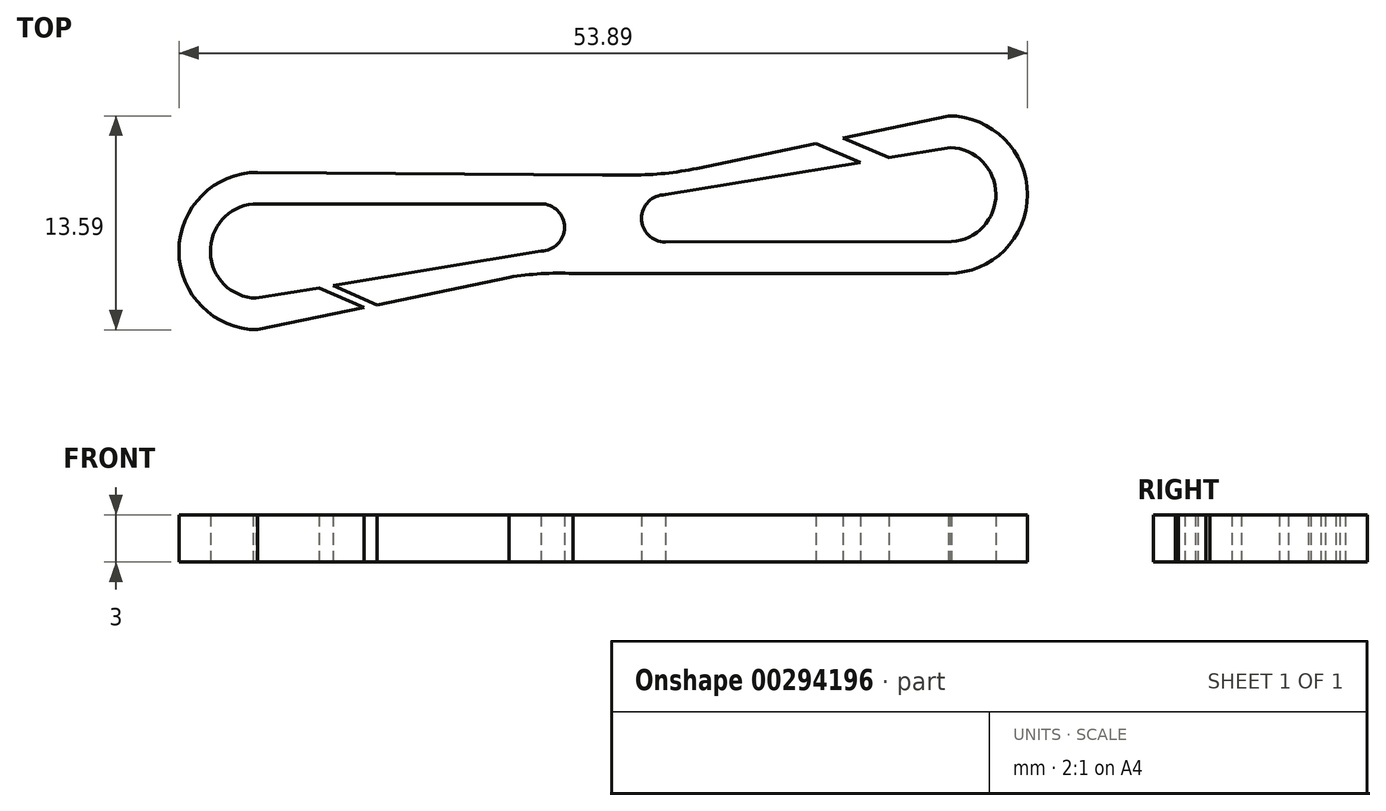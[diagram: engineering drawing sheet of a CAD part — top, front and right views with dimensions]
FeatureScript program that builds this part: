
annotation { "Feature Type Name" : "Feature", "Feature Type Description" : "" }
export const myFeature = defineFeature(function(context is Context, id is Id, definition is map)
    precondition{}
    {
        {
            var Q0;
            Q0=qCreatedBy(makeId("Top.planeOp"),FACE);
            var sketch = newSketch(context, id + "F0", { "sketchPlane" : qUnion([Q0])});
            skLineSegment(sketch, "E0.bottom", {"start": v(0, 0) * mm, "end": v(22, 0) * mm});
            skArc(sketch, "E1", {"start": v(22, 0) * mm, "mid": v(27, 5) * mm, "end": v(22, 10) * mm});
            skLineSegment(sketch, "E2.0", {"start": v(4, 0.17) * mm, "end": v(4, 6.83) * mm, "construction": true});
            skArc(sketch, "E3", {"start": v(4, 5) * mm, "mid": v(2.5, 3.5) * mm, "end": v(4, 2) * mm});
            skLineSegment(sketch, "E4", {"start": v(22, 10) * mm, "end": v(15.3, 8.61) * mm});
            skLineSegment(sketch, "E5", {"start": v(1.94, 6.26) * mm, "end": v(0, 6.26) * mm});
            skArc(sketch, "E6.0", {"start": v(22.2, 2.01) * mm, "mid": v(25, 5.05) * mm, "end": v(22.11, 8) * mm});
            skLineSegment(sketch, "E7", {"start": v(22.11, 8) * mm, "end": v(18.21, 7.36) * mm});
            skLineSegment(sketch, "E8", {"start": v(22.2, 2.01) * mm, "end": v(4, 2) * mm});
            skLineSegment(sketch, "E9", {"start": v(15.3, 8.61) * mm, "end": v(18.21, 7.36) * mm});
            skLineSegment(sketch, "E10.0", {"start": v(13.59, 8.25) * mm, "end": v(16.39, 7.05) * mm});
            skLineSegment(sketch, "E11.trimOffspring", {"start": v(13.59, 8.25) * mm, "end": v(6.02, 6.68) * mm});
            skLineSegment(sketch, "E12.trimOffspring", {"start": v(16.39, 7.05) * mm, "end": v(4, 5) * mm});
            skPoint(sketch, "E13.visualSharp", {"position": v(4, 6.26) * mm});
            skArc(sketch, "E13.filletArc", {"start": v(1.94, 6.26) * mm, "mid": v(3.99, 6.36) * mm, "end": v(6.02, 6.68) * mm});
            skArc(sketch, "E14.1.0", {"start": v(-1.84, 0) * mm, "mid": v(-3.88, -0.02) * mm, "end": v(-5.9, -0.25) * mm});
            skArc(sketch, "E14.1.1", {"start": v(-21.9, 6.42) * mm, "mid": v(-26.9, 1.42) * mm, "end": v(-21.9, -3.58) * mm});
            skArc(sketch, "E14.1.2", {"start": v(-3.9, 1.42) * mm, "mid": v(-2.4, 2.92) * mm, "end": v(-3.9, 4.42) * mm});
            skLineSegment(sketch, "E14.1.3", {"start": v(-3.9, 6.26) * mm, "end": v(-3.9, -0.4) * mm, "construction": true});
            skLineSegment(sketch, "E14.1.5", {"start": v(0, 6.26) * mm, "end": v(-21.9, 6.42) * mm});
            skLineSegment(sketch, "E14.1.6", {"start": v(-17.1, -0.76) * mm, "end": v(-3.9, 1.42) * mm});
            skPoint(sketch, "E14.1.7", {"position": v(-3.9, 0.18) * mm});
            skLineSegment(sketch, "E14.1.8", {"start": v(-21.9, -3.58) * mm, "end": v(-15.14, -2.17) * mm});
            skLineSegment(sketch, "E14.1.9", {"start": v(-1.84, 0) * mm, "end": v(0, 0) * mm});
            skArc(sketch, "E14.1.10", {"start": v(-22.17, 4.41) * mm, "mid": v(-24.89, 1.34) * mm, "end": v(-22, -1.57) * mm});
            skLineSegment(sketch, "E14.1.11", {"start": v(-22, -1.57) * mm, "end": v(-18, -0.91) * mm});
            skLineSegment(sketch, "E14.1.12", {"start": v(-22.17, 4.41) * mm, "end": v(-3.9, 4.42) * mm});
            skLineSegment(sketch, "E14.1.13", {"start": v(-14.3, -2) * mm, "end": v(-5.9, -0.25) * mm});
            skLineSegment(sketch, "E14.1.14", {"start": v(-15.14, -2.17) * mm, "end": v(-18, -0.91) * mm});
            skLineSegment(sketch, "E14.1.15", {"start": v(-14.3, -2) * mm, "end": v(-17.1, -0.76) * mm});
            skPoint(sketch, "E14.center", {"position": v(0, 6.25) * mm});
            skSolve(sketch);
        }
        {
            var Q0;
            Q0=makeQuery(id+"F0.imprint","IMPRINT",FACE,{"disambiguationData":[TD([[makeQuery(id+"F0.imprint","IMPRINT",EDGE,{"derivedFrom":sQuery(id+"F0.wireOp",EDGE,"E0.bottom")}),1.0]])]});
            extrude(context, id + "F1", {"entities" : qUnion([Q0]), "depth" : 3 * mm});
        }
    });
